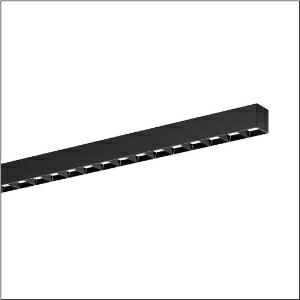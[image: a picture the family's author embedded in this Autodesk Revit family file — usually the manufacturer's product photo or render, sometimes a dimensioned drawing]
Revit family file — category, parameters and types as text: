
# Revit family: silica_r__21_51mx24tctab_feaf
name_source: partatom
category: Lighting Fixtures
units: mm (PartAtom-declared; Revit-internal decimal feet)

## family parameters
Cut with Voids When Loaded = No
Host = Face
Light Source = No
Part Type = Normal
Room Calculation Point = No
Round Connector Dimension = Use Diameter
Shared = No

## types (1)
- --- (1 x LED, 8200 lm, 81.1 W, 6500K)
    Apparent Load = 81 VA
    CIE Flux Codes = 74 94 99 100 100
    Color Rendering = 80
    Color Temperature = 6500K
    Default Elevation = 1800 mm
    Description = Silica® 21, office luminaire, primary light control with darklight reflector, of PMMA, black, light emission: direct distribution, primary light characteristic: asymmetric, installation type: surface-mounted, LED, rated luminous flux: 8.200lm, luminous efficacy: 96lm/W, light colour: 8tw, colour temperature: 2700..6500K, control gear: ECG DALI, with terminal, 3+2-pole, max. 2.5mm², mains connection: 220..240V, AC, 50/60Hz, rated input power: 85.2W, luminaire housing, of aluminium, jet black (RAL 9005), length: 3.004mm, width: 53mm, height: 53mm, protection rating (complete): IP20, insulation class (complete): insulation class I (protective earthing), certification: CE, permissible operating ambient temperature: 0..+35°C, standard: EN 50419, packaging unit: 1 piece
    Height = 0 mm  [stored 0 ft]
    Lamp = 1 x LED
    Lamp Light Flux = 8200 lm
    Lamp Power = 81.1 W
    Lamp count = 1
    Length = 3004 mm
    Luminous efficacy = 101 lm/W
    Manufacturer = Siteco
    ModVariant = No
    Model = 51MX24TCTAB
    Mounting Place = Ceiling
    Mounting Type = Recessed
    Number of Poles = 1
    OnlyDefault = Yes
    Power Factor = 1
    Product Name = Silica® 21
    Product group = office luminaire | ceiling recessed
    ProductGroupID = 401
    Protection Class = Protection class I
    Protection Degree = IP 20
    RLX_Detail_Level = 1
    RLX_Emergency_Light_Flux = 0 lm
    RLX_Emergency_Type = 0
    RLX_Emergency_Type_DB = No
    RlxData = <blob elided: 61273 chars, md5=d7980638>
    Socket = socket
    Standby Power = 0 W
    System Light Flux = 8200 lm
    System Power = 81 W
    Type Comments = individual setting
    Type Image = l_1313577.jpg
    URL = http://relux.com
    VarID = @adj_089355
    Voltage = 0 V
    Weight = 0.00 kg
    Width = 53 mm

note: [stored X ft] marks values corroborated as IEEE doubles in the binary element streams (Revit-internal decimal feet)

## geometry (parser evidence)
native form markers: Blend x4, Sweep x13
no freeform markers — native parametric forms only
